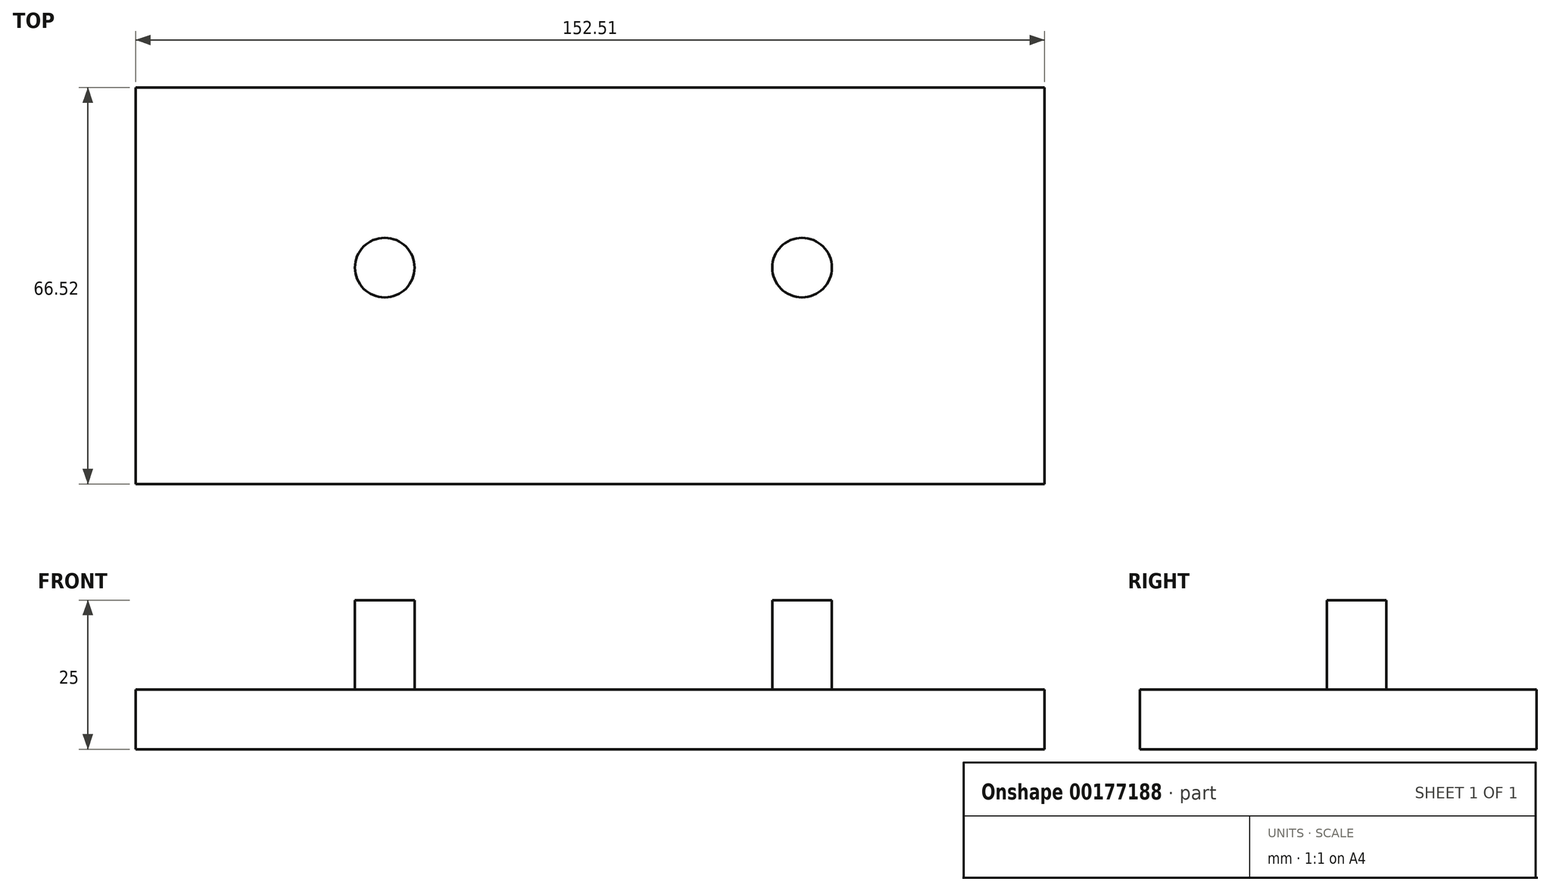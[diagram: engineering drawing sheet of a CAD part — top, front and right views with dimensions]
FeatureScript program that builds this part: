
annotation { "Feature Type Name" : "Feature", "Feature Type Description" : "" }
export const myFeature = defineFeature(function(context is Context, id is Id, definition is map)
    precondition{}
    {
        {
            var Q0;
            Q0=qCreatedBy(makeId("Top.planeOp"),FACE);
            var sketch = newSketch(context, id + "F0", { "sketchPlane" : qUnion([Q0])});
            skLineSegment(sketch, "E0.bottom", {"start": v(-76.8, 30.2) * mm, "end": v(75.7, 30.2) * mm});
            skLineSegment(sketch, "E0.top", {"start": v(-76.8, -36.32) * mm, "end": v(75.7, -36.32) * mm});
            skLineSegment(sketch, "E0.left", {"start": v(-76.8, 30.2) * mm, "end": v(-76.8, -36.32) * mm});
            skLineSegment(sketch, "E0.right", {"start": v(75.7, 30.2) * mm, "end": v(75.7, -36.32) * mm});
            skSolve(sketch);
        }
        {
            var Q0;
            Q0 = qSketchRegion(id + "F0", true);
            extrude(context, id + "F1", {"entities" : qUnion([Q0]), "depth" : 10 * mm});
        }
        {
            var Q0;
            Q0=makeQuery(id+"F1.opExtrude","CAP_FACE",FACE,{"disambiguationData":[OSD([sQuery(id+"F0.wireOp",EDGE,"E0.bottom"),sQuery(id+"F0.wireOp",EDGE,"E0.top"),sQuery(id+"F0.wireOp",EDGE,"E0.left"),sQuery(id+"F0.wireOp",EDGE,"E0.right")])],"isStart":false});
            var sketch = newSketch(context, id + "F2", { "sketchPlane" : qUnion([Q0])});
            skSolve(sketch);
        }
        {
            var Q0;
            Q0=makeQuery(id+"F2.imprint","IMPRINT",FACE,{"disambiguationData":[TD([[makeQuery(id+"F2.imprint","IMPRINT",EDGE,{"derivedFrom":makeQuery(id+"F1.opExtrude","CAP_EDGE",EDGE,{"disambiguationData":[OSD([sQuery(id+"F0.wireOp",EDGE,"E0.bottom")])],"isStart":false})}),-1.0]])]});
            var sketch = newSketch(context, id + "F3", { "sketchPlane" : qUnion([Q0])});
            skCircle(sketch, "E1", {"center": v(-35, 0) * mm, "radius": 5 * mm});
            skCircle(sketch, "E2", {"center": v(35, 0) * mm, "radius": 5 * mm});
            skSolve(sketch);
        }
        {
            var Q0;
            Q0 = qSketchRegion(id + "F3", true);
            extrude(context, id + "F4", {"entities" : qUnion([Q0]), "operationType" : NewBodyOperationType.ADD, "depth" : 15 * mm});
        }
    });
